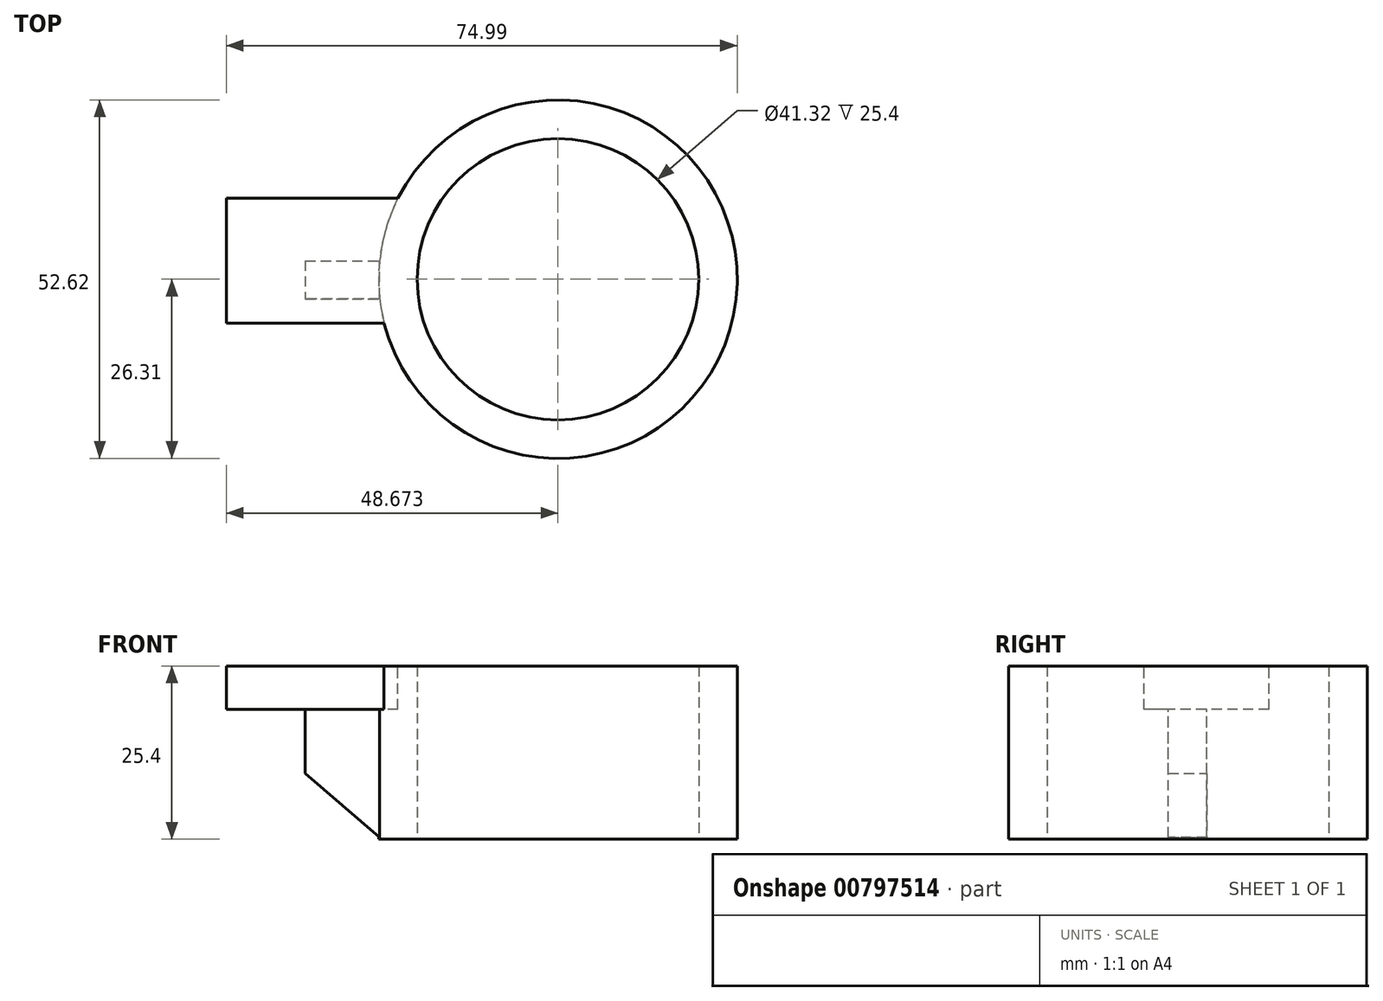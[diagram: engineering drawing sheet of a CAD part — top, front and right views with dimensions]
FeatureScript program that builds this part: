
annotation { "Feature Type Name" : "Feature", "Feature Type Description" : "" }
export const myFeature = defineFeature(function(context is Context, id is Id, definition is map)
    precondition{}
    {
        {
            var Q0;
            Q0=qCreatedBy(makeId("Top.planeOp"),FACE);
            var sketch = newSketch(context, id + "F0", { "sketchPlane" : qUnion([Q0])});
            skCircle(sketch, "E0", {"center": v(21.76, -2.72) * mm, "radius": 26.31 * mm});
            skSolve(sketch);
        }
        {
            var Q0;
            Q0=makeQuery(id+"F0.imprint","IMPRINT",FACE,{"disambiguationData":[TD([[makeQuery(id+"F0.imprint","IMPRINT",EDGE,{"derivedFrom":sQuery(id+"F0.wireOp",EDGE,"E0")}),1.0]])]});
            extrude(context, id + "F1", {"entities" : qUnion([Q0]), "depth" : 25.4 * mm, "offsetDistance" : 25.4 * mm});
        }
        {
            var Q0;
            Q0=makeQuery(id+"F1.opExtrude","CAP_FACE",FACE,{"disambiguationData":[OSD([sQuery(id+"F0.wireOp",EDGE,"E0")])],"isStart":false});
            var sketch = newSketch(context, id + "F2", { "sketchPlane" : qUnion([Q0])});
            skLineSegment(sketch, "E1.bottom", {"start": v(18.1, 9.15) * mm, "end": v(-26.91, 9.15) * mm});
            skLineSegment(sketch, "E1.top", {"start": v(18.1, -9.15) * mm, "end": v(-26.91, -9.15) * mm});
            skLineSegment(sketch, "E1.left", {"start": v(18.1, 9.15) * mm, "end": v(18.1, -9.15) * mm});
            skLineSegment(sketch, "E1.right", {"start": v(-26.91, 9.15) * mm, "end": v(-26.91, -9.15) * mm});
            skPoint(sketch, "E1.middle", {"position": v(-4.4, 0) * mm});
            skSolve(sketch);
        }
        {
            var Q0;
            Q0=makeQuery(id+"F1.opExtrude","CAP_FACE",FACE,{"disambiguationData":[OSD([sQuery(id+"F0.wireOp",EDGE,"E0")])],"isStart":true});
            var sketch = newSketch(context, id + "F3", { "sketchPlane" : qUnion([Q0])});
            skCircle(sketch, "E2", {"center": v(21.76, 2.72) * mm, "radius": 20.66 * mm});
            skSolve(sketch);
        }
        {
            var Q0;
            Q0=makeQuery(id+"F3.imprint","IMPRINT",FACE,{"disambiguationData":[TD([[makeQuery(id+"F3.imprint","IMPRINT",EDGE,{"derivedFrom":sQuery(id+"F3.wireOp",EDGE,"E2")}),1.0]])]});
            extrude(context, id + "F4", {"entities" : qUnion([Q0]), "operationType" : NewBodyOperationType.REMOVE, "endBound" : BoundingType.THROUGH_ALL, "oppositeDirection" : true, "depth" : 25.4 * mm, "offsetDistance" : 25.4 * mm});
        }
        {
            var Q0;
            {var subQ0=sQuery(id+"F2.wireOp",EDGE,"E1.right");Q0=makeQuery(id+"F2.imprint","IMPRINT",FACE,{"disambiguationData":[TD([[makeQuery(id+"F2.imprint","IMPRINT",EDGE,{"derivedFrom":subQ0}),1.0]])]});}
            extrude(context, id + "F5", {"entities" : qUnion([Q0]), "operationType" : NewBodyOperationType.ADD, "oppositeDirection" : true, "depth" : 6.35 * mm, "offsetDistance" : 25.4 * mm});
        }
        {
            var Q0;
            Q0=makeQuery(id+"F5.opExtrude","CAP_FACE",FACE,{"disambiguationData":[OSD([sQuery(id+"F0.wireOp",EDGE,"E0"),sQuery(id+"F2.wireOp",EDGE,"E1.bottom"),sQuery(id+"F2.wireOp",EDGE,"E1.top"),sQuery(id+"F2.wireOp",EDGE,"E1.right")])],"isStart":false});
            var sketch = newSketch(context, id + "F6", { "sketchPlane" : qUnion([Q0])});
            skPoint(sketch, "E3.firstSnap0", {"position": v(-15.33, 9.15) * mm});
            skPoint(sketch, "E3.oppositeSnap0", {"position": v(-4.39, -0.18) * mm});
            skLineSegment(sketch, "E3.bottom", {"start": v(-15.33, 0) * mm, "end": v(-4.39, 0) * mm});
            skLineSegment(sketch, "E3.top", {"start": v(-15.33, 5.62) * mm, "end": v(-4.39, 5.62) * mm});
            skLineSegment(sketch, "E3.left", {"start": v(-15.33, 0) * mm, "end": v(-15.33, 5.62) * mm});
            skLineSegment(sketch, "E3.right", {"start": v(-4.39, 0) * mm, "end": v(-4.39, 5.62) * mm});
            skSolve(sketch);
        }
        {
            var Q0;
            {var subQ4=sQuery(id+"F6.wireOp",EDGE,"E3.top");Q0=makeQuery(id+"F6.imprint","IMPRINT",FACE,{"disambiguationData":[TD([[makeQuery(id+"F6.imprint","IMPRINT",EDGE,{"derivedFrom":subQ4}),-1.0]])]});}
            extrude(context, id + "F7", {"entities" : qUnion([Q0]), "operationType" : NewBodyOperationType.ADD, "depth" : 18.8 * mm, "offsetDistance" : 25.4 * mm});
        }
        {
            var Q0;
            Q0=makeQuery(id+"F7.opExtrude","SWEPT_FACE",FACE,{"disambiguationData":[OSD([sQuery(id+"F6.wireOp",EDGE,"E3.bottom")])]});
            var sketch = newSketch(context, id + "F8", { "sketchPlane" : qUnion([Q0])});
            skLineSegment(sketch, "E4", {"start": v(15.33, 9.65) * mm, "end": v(4.4, 9.65) * mm});
            skLineSegment(sketch, "E5", {"start": v(15.33, 9.65) * mm, "end": v(4.4, 0.25) * mm});
            skSolve(sketch);
        }
        {
            var Q0;
            {var subQ0=sQuery(id+"F8.wireOp",EDGE,"E5");Q0=makeQuery(id+"F8.imprint","IMPRINT",FACE,{"disambiguationData":[TD([[makeQuery(id+"F8.imprint","IMPRINT",EDGE,{"derivedFrom":subQ0}),1.0]])]});}
            extrude(context, id + "F9", {"entities" : qUnion([Q0]), "operationType" : NewBodyOperationType.REMOVE, "endBound" : BoundingType.THROUGH_ALL, "oppositeDirection" : true, "depth" : 25.4 * mm, "offsetDistance" : 25.4 * mm});
        }
    });
